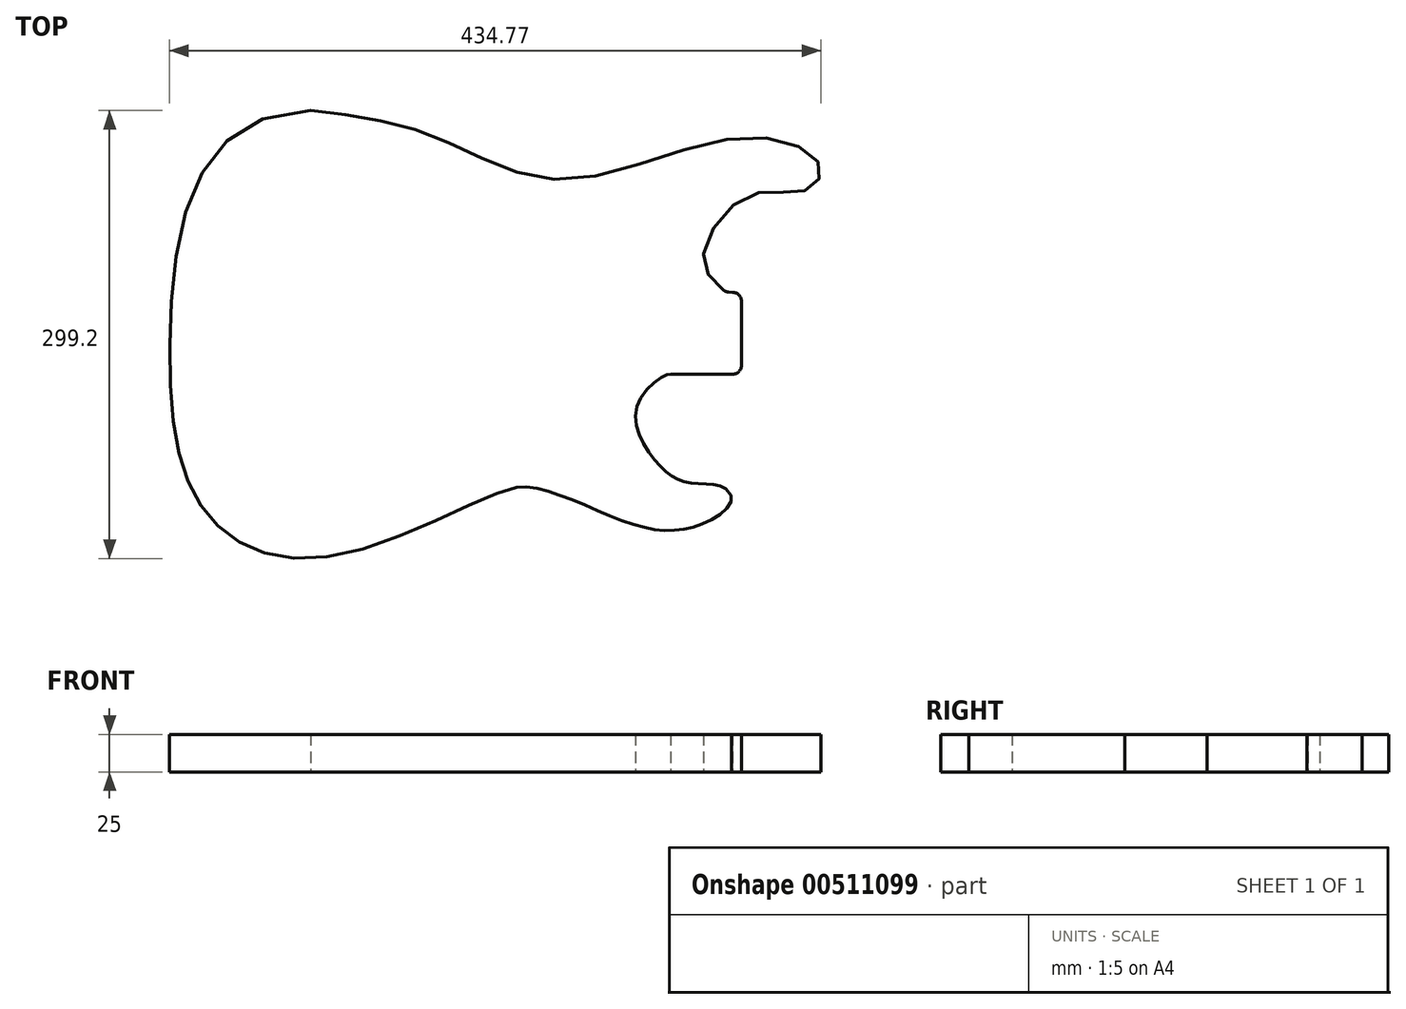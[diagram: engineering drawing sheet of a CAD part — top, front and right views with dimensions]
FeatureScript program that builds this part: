
annotation { "Feature Type Name" : "Feature", "Feature Type Description" : "" }
export const myFeature = defineFeature(function(context is Context, id is Id, definition is map)
    precondition{}
    {
        {
            var Q0;
            Q0=qCreatedBy(makeId("Top.planeOp"),FACE);
            var sketch = newSketch(context, id + "F0", { "sketchPlane" : qUnion([Q0])});
            skFitSpline(sketch, "E0", {"points": [v(99.79, 309.99) * mm, v(5.9, 159.62) * mm, v(30.48, 40.68) * mm, v(114.8, 12.45) * mm, v(237.43, 58.24) * mm], "startDerivative": vector(-836.75, -8.74) * mm, "endDerivative": vector(239.24, 34.73) * mm});
            skFitSpline(sketch, "E1", {"points": [v(237.43, 58.24) * mm, v(313.21, 34.26) * mm, v(364.46, 35.35) * mm, v(377.11, 57.32) * mm], "startDerivative": vector(140.14, 20.34) * mm, "endDerivative": vector(-126.7, 96.54) * mm});
            skFitSpline(sketch, "E2", {"points": [v(377.11, 57.32) * mm, v(352.8, 61.45) * mm, v(331.58, 74.4) * mm, v(318.08, 113.53) * mm, v(340.43, 133.78) * mm], "startDerivative": vector(-75.91, 57.84) * mm, "endDerivative": vector(37.7, -19.75) * mm});
            skFitSpline(sketch, "E3", {"points": [v(377.11, 188.85) * mm, v(362.16, 212.74) * mm, v(393.54, 253.62) * mm, v(430.04, 256.54) * mm, v(440.26, 271.87) * mm, v(393.54, 292.3) * mm, v(268, 263.84) * mm, v(181.21, 293.16) * mm, v(99.79, 309.99) * mm], "startDerivative": vector(-282.83, 211.8) * mm, "endDerivative": vector(-544.24, 62.8) * mm});
            skLineSegment(sketch, "E4.left", {"start": v(387.7, 182.3) * mm, "end": v(387.7, 140.13) * mm});
            skPoint(sketch, "E5.visualSharp", {"position": v(387.7, 188.65) * mm});
            skArc(sketch, "E5.filletArc", {"start": v(387.7, 182.3) * mm, "mid": v(386.54, 185.96) * mm, "end": v(383.49, 188.28) * mm});
            skPoint(sketch, "E6.visualSharp", {"position": v(387.7, 133.78) * mm});
            skArc(sketch, "E6.filletArc", {"start": v(381.35, 133.78) * mm, "mid": v(385.84, 135.64) * mm, "end": v(387.7, 140.13) * mm});
            skArc(sketch, "E7", {"start": v(383.49, 188.28) * mm, "mid": v(382.6, 188.52) * mm, "end": v(381.7, 188.64) * mm});
            skLineSegment(sketch, "E8", {"start": v(381.7, 188.64) * mm, "end": v(381.7, 188.64) * mm});
            skLineSegment(sketch, "E9", {"start": v(340.43, 133.78) * mm, "end": v(381.35, 133.78) * mm});
            skArc(sketch, "E10.filletArc", {"start": v(375.48, 190.1) * mm, "mid": v(377.19, 189.15) * mm, "end": v(379.1, 188.76) * mm});
            skFitSpline(sketch, "E11", {"points": [v(379.1, 188.76) * mm, v(381.7, 188.64) * mm], "startDerivative": vector(2.61, -0.12) * mm, "endDerivative": vector(2.61, -0.12) * mm});
            skSolve(sketch);
        }
        {
            var Q0;
            Q0 = qSketchRegion(id + "F0", true);
            extrude(context, id + "F1", {"entities" : qUnion([Q0]), "depth" : 25 * mm});
        }
    });
